# Revit family: 94540 051_Gold
name_source: partatom
category: Modelos genéricos
units: mm (PartAtom-declared; Revit-internal decimal feet)

## family parameters
Compartilhado = Sim
Corte com vazios quando carregada = Não
Cota do conector redondo = Utilizar diâmetro
Pode hospedar o vergalhão = Não
Ponto de cálculo do ambiente = Não
Sempre na vertical = Não
Tipo de parte = Não definido

## types (1)
- 94540 051_Gold
    Aramado Interno para saco de lixo = Sim
    Balde plástico removível = Não
    Capacidade = 5L
    Elevação padrão = 0 mm  [stored 0 ft]
    Espessura da tampa = 1 mm
    Marca = Tramontina
    Material = Aço Inox AISI 304 com acabamento Scotch Brite com revestimento Gold
    Modelo = Lixeira Tramontina Útil em Aço Inox com Acabamento Scotch Brite e revestimento a base de verniz Gold 5 L
    Referência = 94540/051
    Saco de lixo recomendado = 5-10L
    Tratamento antidigitais = Não

note: [stored X ft] marks values corroborated as IEEE doubles in the binary element streams (Revit-internal decimal feet)
